# Revit family: 64442219
name_source: partatom
category: Plumbing Fixtures
units: mm (PartAtom-declared; Revit-internal decimal feet)

## family parameters
Always vertical = Yes
Cut with Voids When Loaded = No
OmniClass Number = 23.45.55.00
OmniClass Title = Sanitary Faucets, Wastes
Part Type = Normal
Room Calculation Point = No
Round Connector Dimension = Use Diameter
Shared = No
Work Plane-Based = No

## types (1)
- 64442219 Washbasin faucet, 6 V, Bluetooth
    2D/3D/BIM Files URL = http://static.hansa.com
    3D View = https://static.hansa.com
    Advanced Features = Software settings adjustable via App
    Aerator = Hidden aerator
    Afterflow Period = 3 s (1-20 s)
    Ambience photo = http://static.hansa.com
    AssetType = Fixed
    Automatic Flush Frequency = off (off/1-120 h)
    Automatic Flush Period = 30 s (1-1800 s)
    BIMObjectName = 64442219
    Backflow Prevention EN1717 = AA
    Battery = Lithium 2CR5 6 V
    Bluetooth = 4.x (D034445)
    BodyMaterial = Brass
    Brand = HANSA
    Catalog Drawing URL = http://static.hansa.com
    Category = Washbasin
    CloseOffRating = 0
    Color = Chrome
    Connection = Flexible inlet pipes
    Connection Size = G3/8
    Constituents = Single lever
    Default Elevation = 0 mm  [stored 0 ft]
    Dimension Drawing URL = http://static.hansa.com
    DurationUnit = Year
    EAN Number = 4057304015069
    EMC Directive = Radio Equipment Directive 2014/53/EU , 
Low Voltage Directive 2014/35/EU , 
EMC Directive 2014/30/EU , 
RoHS Directive 2011/65/EU
    EN Standard = EN 15091,
ETSI EN 301 489-1 V1.9.2 , 
ETSI EN 300 328 v2.2.2 , 
EN 61000-6-1:2007 , 
EN 61000-6-3:2007+A1:2011+AC:2012 , 
EN 60335-1:2012+A11+A13+A1+A14+A2+A15:2021, Part 19.11.4
    ETIM Class Number = EC010340 Electronic tap
    Electronic Parts = Autofocus infrared sensor;Solenoid valve;Low battery indicator
    Excluded Items = Without pop-up waste;Without draw-rod opening
    FDV Document URL = http://www.hansa.com
    FaucetMainMaterial = Brass
    Features = Touchless;Bluetooth®;Battery-operated
    Finish = Polished
    Flow Drawing URL = http://static.hansa.com
    Flow Rate At 300kPa = 0.1 L/s
    FlowCoefficient = 0
    Group = Washbasin faucet
    IfcExportAs = IfcValveType
    IfcExportType = FAUCET
    InletConnectionSize = 10 mm  [stored 0.0328084 ft]
    Installation Type = Deck mounted
    Installation and Maintenance Guide URL = http://static.hansa.com
    Interactive AR View URL = https://static.hansa.com
    Lever Handle = Temperature control handle
    Manufacturer = HANSA
    ManufacturerName = HANSA
    ManufacturerURL = http://www.hansa.com
    Market = International;Germany;Austria;Belgium;Netherlands;France;Czech Republic;Slovakia;Italy;Spain
    Material = Brass
    Max Flow Period = 2 min (1 - 1800 s)
    Max. Hot Water Supply = 70 °C
    Mechanical Parts = Mixing valve for manual temperature control;Non-return valve(s);Litter filter(s)
    Mobile Product Information URL = http://mpi.hansa.com
    Model = 64442219 Washbasin faucet, 6 V, Bluetooth
    ModelReference = 64442219
    Mounting Holes = 1 hole
    NBSDescription = Water supply fittings for wash basins and troughs
    NBSReference = 45-35-70/371
    Name = 64442219 Washbasin faucet, 6 V, Bluetooth
    Name_en = 64442219 Washbasin faucet, 6 V, Bluetooth
    NominalDepth = 212 mm
    NominalHeight = 293 mm
    NominalWidth = 72 mm
    Operating Distance = 20-180 mm (150/180/250 mm)
    Operating Voltage = 6 V
    Product Code = 64442219
    Product Family = HANSAELECTRA
    Product Image URL = http://static.hansa.com
    Product URL = http://static.hansa.com
    Protection Class = IP 55
    Sales Package dimensions (LxWxH) = 695 x 320 x 85
    Shape = Sculptured
    Size = 70x210x295 mm
    Spare-Part Information URL = http://static.hansa.com
    Spout Projection = 170 mm
    Spout Type = Fixed spout
    Surface treatment = Chrome
    Technical DataSheet URL = http://www.hansa.com
    Temperature = Temperature fixable;Temperature limiter (retrofittable)
    Temperature Adjustments = Temperature preset fixable;Adjustable hot water stop (included, retrofittable)
    UNSPSC Class Number = 30181700 Faucets or taps
    URL Declaration Of Performance (DOP) = http://static.hansa.com
    URL Declaration of Asbestos = http://static.hansa.com
    URL Declaration of Conformity = http://static.hansa.com
    URL Declaration of SCIP = http://static.hansa.com
    URL EU Packaging Declaration = http://static.hansa.com
    URL EcoLabel Declaration = http://static.hansa.com
    URL Materials Declaration = http://www.hansa.com
    URL REACH = http://static.hansa.com
    URL UN38.3 = http://static.hansa.com
    URL WEEE = http://static.hansa.com
    Uniclass2 = Pr_40_30_96_96
    Uniclass2015Description = Washbasin manual water supply sets
    Uniclass2015Reference = Pr_40_20_87_96
    Version = 1
    VersionDate = 01/06/2023
    Warranty Information URL = http://warranty.hansa.com
    WarrantyDescription = http://warranty.hansa.com
    WarrantyDurationUnit = Year
    Working Pressure = 100 - 1000 kPa

note: [stored X ft] marks values corroborated as IEEE doubles in the binary element streams (Revit-internal decimal feet)

## geometry (parser evidence)
native form markers: Sweep x5
no freeform markers — native parametric forms only
